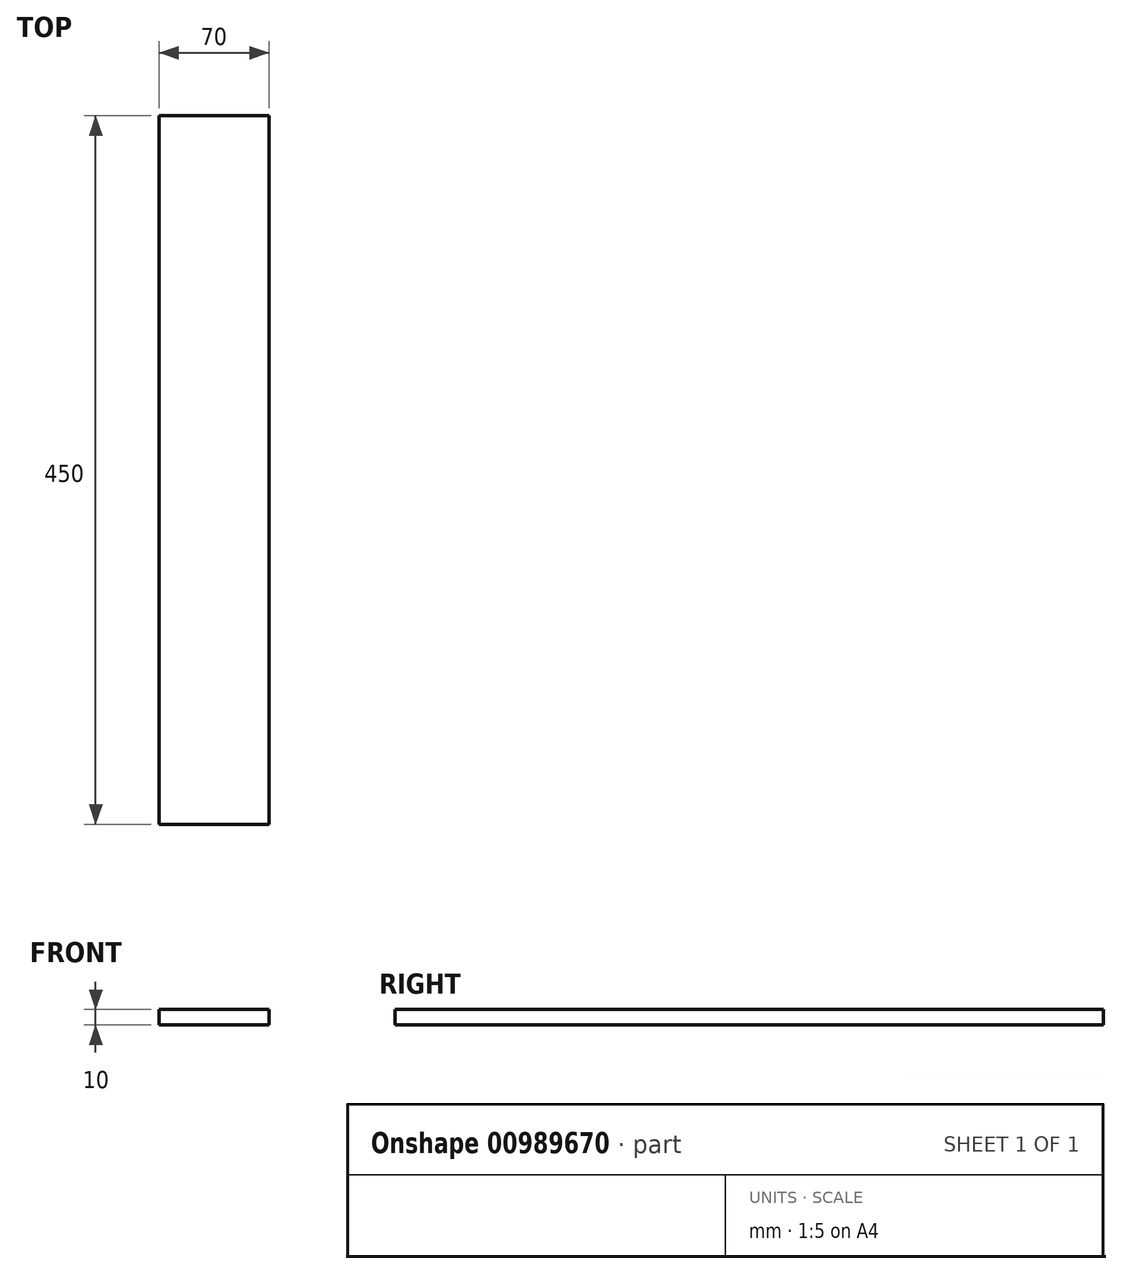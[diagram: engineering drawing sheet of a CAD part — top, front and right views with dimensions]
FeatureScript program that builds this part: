
annotation { "Feature Type Name" : "Feature", "Feature Type Description" : "" }
export const myFeature = defineFeature(function(context is Context, id is Id, definition is map)
    precondition{}
    {
        {
            var Q0;
            Q0=qCreatedBy(makeId("Front.planeOp"),FACE);
            var sketch = newSketch(context, id + "F0", { "sketchPlane" : qUnion([Q0])});
            skLineSegment(sketch, "E0.bottom", {"start": v(0, 0) * mm, "end": v(70, 0) * mm});
            skLineSegment(sketch, "E0.top", {"start": v(0, 10) * mm, "end": v(70, 10) * mm});
            skLineSegment(sketch, "E0.left", {"start": v(0, 0) * mm, "end": v(0, 10) * mm});
            skLineSegment(sketch, "E0.right", {"start": v(70, 0) * mm, "end": v(70, 10) * mm});
            skSolve(sketch);
        }
        {
            var Q0;
            Q0 = qSketchRegion(id + "F0", true);
            extrude(context, id + "F1", {"entities" : qUnion([Q0]), "depth" : 450 * mm, "offsetDistance" : 25 * mm});
        }
    });
